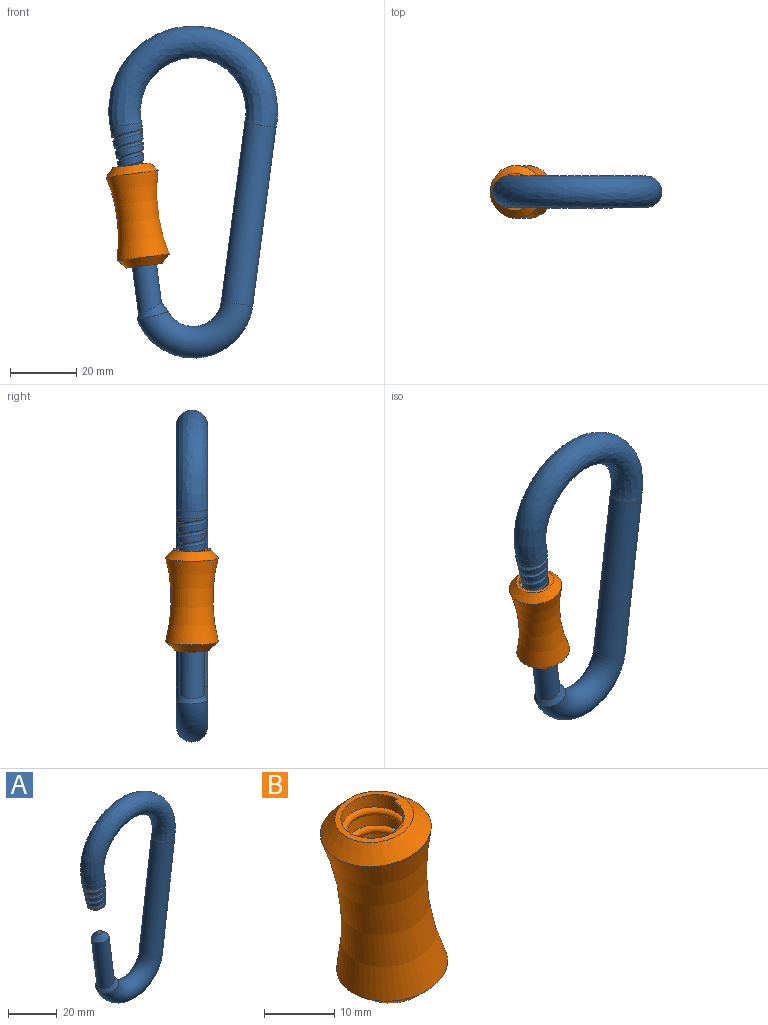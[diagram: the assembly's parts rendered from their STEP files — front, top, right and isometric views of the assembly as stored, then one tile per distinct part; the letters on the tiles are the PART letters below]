
ASSEMBLY  parts=2 mates=1
PART A: 13 faces, bbox 51.1x9.8x101.6 mm
  f0: cylinder r=4.76mm len=9.75mm, axis (-0.13,0,0.99), area 64.9mm2, adj f3,f4,f5,f6
  f1: torus R=13.3mm, axis (0,1,0), area 1052.5mm2, adj f2,f12
  f2: cylinder r=4.76mm len=55.02mm, axis (-0.13,0,-0.99), area 1623.1mm2, adj f1,f3
  f3: bspline ~50.87x30.98mm, area 2208.6mm2, adj f0,f2
  f4: cone r=4.76mm half-angle=5deg, axis (-0.13,0,0.99), area 197mm2, adj f0,f5,f6,f9
  f5: plane 1.49x0.89mm, normal (0,-1,0), area 0.6mm2, adj f0,f4,f6
  f6: bspline ~14.01x9.81mm, area 188mm2, adj f0,f4,f5,f9
  f7: cylinder r=3.65mm len=25.82mm, axis (-0.13,0,0.99), area 544mm2, adj f11,f12
  f8: plane 2.22x2.2mm, normal (-0.13,0,0.99), area 3.9mm2, adj f11
  f9: torus R=3.65mm, axis (0.13,0,-0.99), area 16.3mm2, adj f4,f6,f10
  f10: plane 6.03x5.98mm, normal (0.13,0,-0.99), area 28.6mm2, adj f9
  f11: cone r=1.11mm half-angle=45deg, axis (0.13,0,-0.99), area 53.7mm2, adj f7,f8
  f12: bspline ~9.54x9.38mm, area 67.1mm2, adj f1,f7
PART B: 12 faces, bbox 53.2x44.5x75.1 mm
  f0: plane 0.66x0.64mm, normal (0,1,0), area 0.3mm2, adj f1,f2,f3
  f1: bspline ~14.01x9.81mm, area 185.8mm2, adj f0,f2,f3,f6,f7
  f2: cone r=4.76mm half-angle=85deg, axis (0.13,0,-0.99), area 31.2mm2, adj f0,f1,f3,f9
  f3: cone r=4.76mm half-angle=5deg, axis (-0.13,0,0.99), area 206.9mm2, adj f0,f1,f2,f6,f7
  f4: plane 10.82x10.72mm, normal (0.13,0,-0.99), area 15.8mm2, adj f5,f10
  f5: cone r=3.65mm half-angle=45deg, axis (0.13,0,-0.99), area 42mm2, adj f4,f8
  f6: plane 0.72x0.64mm, normal (0,-1,0), area 0.3mm2, adj f1,f3,f7
  f7: plane 7.68x7.62mm, normal (0.13,0,-0.99), area 6.5mm2, adj f1,f3,f6,f8
  f8: cylinder r=3.84mm len=17.59mm, axis (0.13,0,-0.99), area 404mm2, adj f5,f7
  f9: cone r=7.95mm half-angle=42.5deg, axis (0.13,0,-0.99), area 146.4mm2, adj f2,f11
  f10: cone r=5.41mm half-angle=45deg, axis (-0.13,0,0.99), area 150.7mm2, adj f4,f11
  f11: torus R=55.53mm, axis (0.13,0,-0.99), area 1102.9mm2, adj f9,f10
PLACE A t=(-28.41,-36.38,1.88)mm
PLACE B t=(-27.11,-36.38,-8.04)mm
MATE slider B.f9 <-> A.f4  axis (0.13,0,-0.99) through (-46.71,-36.38,-17.15)mm
